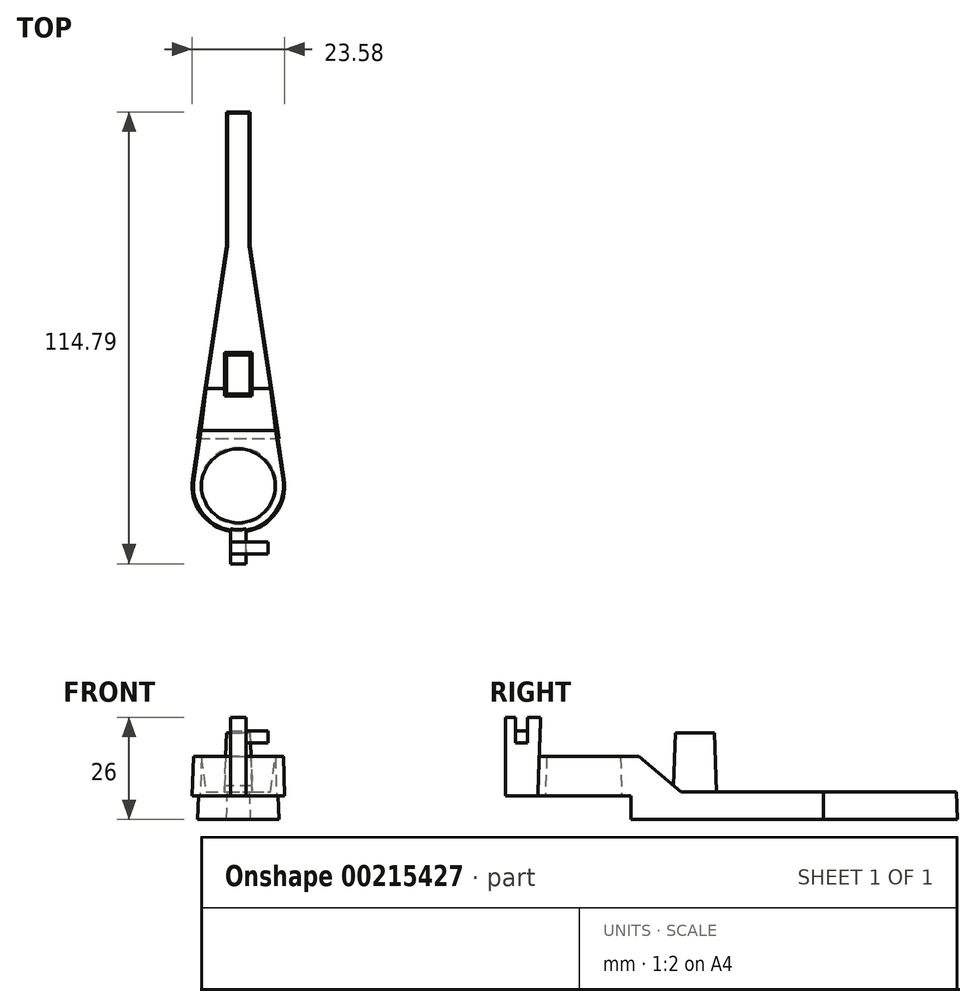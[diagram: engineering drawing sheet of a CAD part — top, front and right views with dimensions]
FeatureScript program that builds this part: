
annotation { "Feature Type Name" : "Feature", "Feature Type Description" : "" }
export const myFeature = defineFeature(function(context is Context, id is Id, definition is map)
    precondition{}
    {
        {
            var Q0;
            Q0=qCreatedBy(makeId("Top.planeOp"),FACE);
            var sketch = newSketch(context, id + "F0", { "sketchPlane" : qUnion([Q0])});
            skCircle(sketch, "E0", {"center": v(0, 0) * mm, "radius": 12 * mm});
            skLineSegment(sketch, "E1", {"start": v(-3, 95) * mm, "end": v(3, 95) * mm});
            skLineSegment(sketch, "E2", {"start": v(0, -12) * mm, "end": v(0, 95) * mm, "construction": true});
            skPoint(sketch, "E3", {"position": v(0, 95) * mm});
            skLineSegment(sketch, "E4", {"start": v(-3, 95) * mm, "end": v(-3, 61) * mm});
            skLineSegment(sketch, "E5", {"start": v(3, 95) * mm, "end": v(3, 61) * mm});
            skLineSegment(sketch, "E6", {"start": v(-3, 61) * mm, "end": v(-11.87, 1.78) * mm});
            skLineSegment(sketch, "E7", {"start": v(3, 61) * mm, "end": v(11.87, 1.78) * mm});
            skSolve(sketch);
        }
        {
            var Q0;
            Q0 = qSketchRegion(id + "F0", true);
            extrude(context, id + "F1", {"entities" : qUnion([Q0]), "depth" : 16 * mm, "hasDraft" : true, "draftAngle" : 2 * degree, "draftPullDirection" : true});
        }
        {
            var Q0;
            Q0=qCreatedBy(makeId("Right.planeOp"),FACE);
            cPlane(context, id + "F2", {"entities" : qUnion([Q0]), "cplaneType" : CPlaneType.OFFSET, "offset" : 12 * mm, "width" : 150 * mm, "height" : 150 * mm});
        }
        {
            var Q0;
            Q0=qCreatedBy(id+"F2.planeOp",FACE);
            var sketch = newSketch(context, id + "F3", { "sketchPlane" : qUnion([Q0])});
            skLineSegment(sketch, "E8", {"start": v(94.76, 7) * mm, "end": v(24.76, 7) * mm});
            skLineSegment(sketch, "E9", {"start": v(24.76, 7) * mm, "end": v(14.03, 16) * mm});
            skLineSegment(sketch, "E10", {"start": v(12, 0) * mm, "end": v(12, 6) * mm});
            skLineSegment(sketch, "E11", {"start": v(12, 6) * mm, "end": v(-11.8, 6) * mm});
            skLineSegment(sketch, "E12", {"start": v(12, 0) * mm, "end": v(-12, 0) * mm});
            skLineSegment(sketch, "E13", {"start": v(-12, 0) * mm, "end": v(-11.8, 6) * mm});
            skLineSegment(sketch, "E14", {"start": v(14.03, 16) * mm, "end": v(94.44, 16) * mm});
            skLineSegment(sketch, "E15", {"start": v(94.44, 16) * mm, "end": v(94.76, 7) * mm});
            skSolve(sketch);
        }
        {
            var Q0;
            Q0 = qSketchRegion(id + "F3", true);
            extrude(context, id + "F4", {"entities" : qUnion([Q0]), "operationType" : NewBodyOperationType.REMOVE, "endBound" : BoundingType.THROUGH_ALL, "oppositeDirection" : true, "depth" : 25 * mm});
        }
        {
            var Q0;
            Q0=makeQuery(id+"F4.boolean.opBoolean","COPY",FACE,{"derivedFrom":makeQuery(id+"F4.opExtrude","SWEPT_FACE",FACE,{"disambiguationData":[OSD([sQuery(id+"F3.wireOp",EDGE,"E8")])]})});
            cPlane(context, id + "F5", {"entities" : qUnion([Q0]), "cplaneType" : CPlaneType.OFFSET, "offset" : 15 * mm, "width" : 150 * mm, "height" : 150 * mm});
        }
        {
            var Q0;
            Q0=qCreatedBy(id+"F5.planeOp",FACE);
            var sketch = newSketch(context, id + "F6", { "sketchPlane" : qUnion([Q0])});
            skLineSegment(sketch, "E16.bottom", {"start": v(-3, 23.3) * mm, "end": v(3, 23.3) * mm});
            skLineSegment(sketch, "E16.top", {"start": v(-3, 33.3) * mm, "end": v(3, 33.3) * mm});
            skLineSegment(sketch, "E16.left", {"start": v(-3, 23.3) * mm, "end": v(-3, 33.3) * mm});
            skLineSegment(sketch, "E16.right", {"start": v(3, 23.3) * mm, "end": v(3, 33.3) * mm});
            skPoint(sketch, "E16.middle", {"position": v(0, 28.3) * mm});
            skSolve(sketch);
        }
        {
            var Q0;
            Q0 = qSketchRegion(id + "F6", true);
            extrude(context, id + "F7", {"entities" : qUnion([Q0]), "operationType" : NewBodyOperationType.ADD, "endBound" : BoundingType.UP_TO_NEXT, "oppositeDirection" : true, "depth" : 25 * mm, "hasDraft" : true, "draftAngle" : 2 * degree});
        }
        {
            var Q0;
            Q0=makeQuery(id+"F4.boolean.opBoolean","COPY",FACE,{"derivedFrom":makeQuery(id+"F4.opExtrude","SWEPT_FACE",FACE,{"disambiguationData":[OSD([sQuery(id+"F3.wireOp",EDGE,"E11")])]})});
            var sketch = newSketch(context, id + "F8", { "sketchPlane" : qUnion([Q0])});
            skCircle(sketch, "E17", {"center": v(0, 0) * mm, "radius": 9.72 * mm});
            skSolve(sketch);
        }
        {
            var Q0;
            Q0 = qSketchRegion(id + "F8", true);
            extrude(context, id + "F9", {"entities" : qUnion([Q0]), "operationType" : NewBodyOperationType.REMOVE, "endBound" : BoundingType.THROUGH_ALL, "oppositeDirection" : true, "depth" : 25 * mm, "hasDraft" : true, "draftAngle" : 2 * degree, "draftPullDirection" : true});
        }
        {
            var Q0;
            Q0=makeQuery(id+"F4.boolean.opBoolean","COPY",FACE,{"derivedFrom":makeQuery(id+"F4.opExtrude","SWEPT_FACE",FACE,{"disambiguationData":[OSD([sQuery(id+"F3.wireOp",EDGE,"E11")])]})});
            var sketch = newSketch(context, id + "F10", { "sketchPlane" : qUnion([Q0])});
            skLineSegment(sketch, "E18", {"start": v(0, 11.8) * mm, "end": v(0, 19.8) * mm, "construction": true});
            skPoint(sketch, "E18.endSnap0", {"position": v(0, 11.8) * mm});
            skLineSegment(sketch, "E19", {"start": v(0, 19.8) * mm, "end": v(-2, 19.8) * mm});
            skLineSegment(sketch, "E20", {"start": v(-2, 19.8) * mm, "end": v(-2, 11.62) * mm});
            skLineSegment(sketch, "E21", {"start": v(0, 19.8) * mm, "end": v(2, 19.8) * mm});
            skLineSegment(sketch, "E22", {"start": v(2, 19.8) * mm, "end": v(2, 11.62) * mm});
            skArc(sketch, "E23", {"start": v(2, 11.62) * mm, "mid": v(0, 11.8) * mm, "end": v(-2, 11.62) * mm});
            skSolve(sketch);
        }
        {
            var Q0;
            Q0=qCreatedBy(makeId("Front.planeOp"),FACE);
            var Q1;
            Q1=sQuery(id+"F10.wireOp",VERTEX,"E21.start");
            cPlane(context, id + "F11", {"entities" : qUnion([Q0, Q1]), "cplaneType" : CPlaneType.PLANE_POINT, "offset" : 25 * mm, "width" : 150 * mm, "height" : 150 * mm});
        }
        {
            var Q0;
            Q0=qCreatedBy(id+"F11.planeOp",FACE);
            var sketch = newSketch(context, id + "F12", { "sketchPlane" : qUnion([Q0])});
            skLineSegment(sketch, "E24.bottom", {"start": v(-2, 6) * mm, "end": v(2, 6) * mm});
            skLineSegment(sketch, "E24.top", {"start": v(-2, 26) * mm, "end": v(2, 26) * mm});
            skLineSegment(sketch, "E24.left", {"start": v(-2, 6) * mm, "end": v(-2, 26) * mm});
            skLineSegment(sketch, "E24.right", {"start": v(2, 6) * mm, "end": v(2, 26) * mm});
            skSolve(sketch);
        }
        {
            var Q0;
            Q0 = qSketchRegion(id + "F12", true);
            var Q1;
            Q1=makeQuery(id+"F1.opExtrude","SWEPT_FACE",FACE,{"disambiguationData":[OSD([sQuery(id+"F0.wireOp",EDGE,"E0")])]});
            extrude(context, id + "F13", {"entities" : qUnion([Q0]), "operationType" : NewBodyOperationType.ADD, "endBound" : BoundingType.UP_TO_SURFACE, "oppositeDirection" : true, "endBoundEntityFace" : qUnion([Q1]), "depth" : 8 * mm});
        }
        {
            var Q0;
            Q0=makeQuery(id+"F13.opExtrude","SWEPT_FACE",FACE,{"disambiguationData":[OSD([sQuery(id+"F12.wireOp",EDGE,"E24.right")])]});
            var sketch = newSketch(context, id + "F14", { "sketchPlane" : qUnion([Q0])});
            skLineSegment(sketch, "E25.bottom", {"start": v(-17.3, 22.5) * mm, "end": v(-14.3, 22.5) * mm});
            skLineSegment(sketch, "E25.top", {"start": v(-17.3, 19.5) * mm, "end": v(-14.3, 19.5) * mm});
            skLineSegment(sketch, "E25.left", {"start": v(-17.3, 22.5) * mm, "end": v(-17.3, 19.5) * mm});
            skLineSegment(sketch, "E25.right", {"start": v(-14.3, 22.5) * mm, "end": v(-14.3, 19.5) * mm});
            skSolve(sketch);
        }
        {
            var Q0;
            Q0 = qSketchRegion(id + "F14", true);
            extrude(context, id + "F15", {"entities" : qUnion([Q0]), "operationType" : NewBodyOperationType.ADD, "depth" : 5.5 * mm});
        }
        {
            var Q0;
            Q0=makeQuery(id+"F13.opExtrude","SWEPT_FACE",FACE,{"disambiguationData":[OSD([sQuery(id+"F12.wireOp",EDGE,"E24.right")])]});
            var sketch = newSketch(context, id + "F16", { "sketchPlane" : qUnion([Q0])});
            skLineSegment(sketch, "E26.bottom", {"start": v(-17.3, 22.5) * mm, "end": v(-14.3, 22.5) * mm});
            skLineSegment(sketch, "E26.top", {"start": v(-17.3, 26) * mm, "end": v(-14.3, 26) * mm});
            skLineSegment(sketch, "E26.left", {"start": v(-17.3, 22.5) * mm, "end": v(-17.3, 26) * mm});
            skLineSegment(sketch, "E26.right", {"start": v(-14.3, 22.5) * mm, "end": v(-14.3, 26) * mm});
            skSolve(sketch);
        }
        {
            var Q0;
            Q0 = qSketchRegion(id + "F16", true);
            extrude(context, id + "F17", {"entities" : qUnion([Q0]), "operationType" : NewBodyOperationType.REMOVE, "endBound" : BoundingType.THROUGH_ALL, "oppositeDirection" : true, "depth" : 25 * mm});
        }
    });
